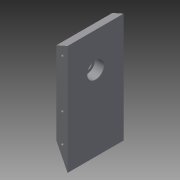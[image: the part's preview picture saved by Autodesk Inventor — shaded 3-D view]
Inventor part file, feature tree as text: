
AUTODESK INVENTOR PART (.ipt)
format: ipt  version: 2015 (Build 190159000, 159)  size: 102,912 bytes
history: native  units: mm
features: extrude x3, sketch x2, plane x1
ambient origin geometry x8: Origin, YZ Plane, XZ Plane, XY Plane, X Axis, Y Axis, Z Axis, Center Point
bodies: Body1 (feature_tree)
feature tree (6):
  sketch  "Sketch1"  dims[d3=10.0mm d4=73.5mm]
  plane  "Work Plane1"
  extrude  "Extrusion3"  Depth=10.0mm
  sketch  "Sketch3"  dims[d6=4.444444mm d8=20.0mm d17=2.5mm d26=2.5mm d28=2.5mm d29=50.0mm d30=0.0mm d37=26.5mm d38=25.0mm d39=15.0mm d40=10.0mm d41=0.0mm d42=10.0mm d43=2.0mm d44=0.0mm]
  extrude  "Extrusion6"  Depth=2.0mm
  extrude  "Extrusion7"  Depth=2.0mm
